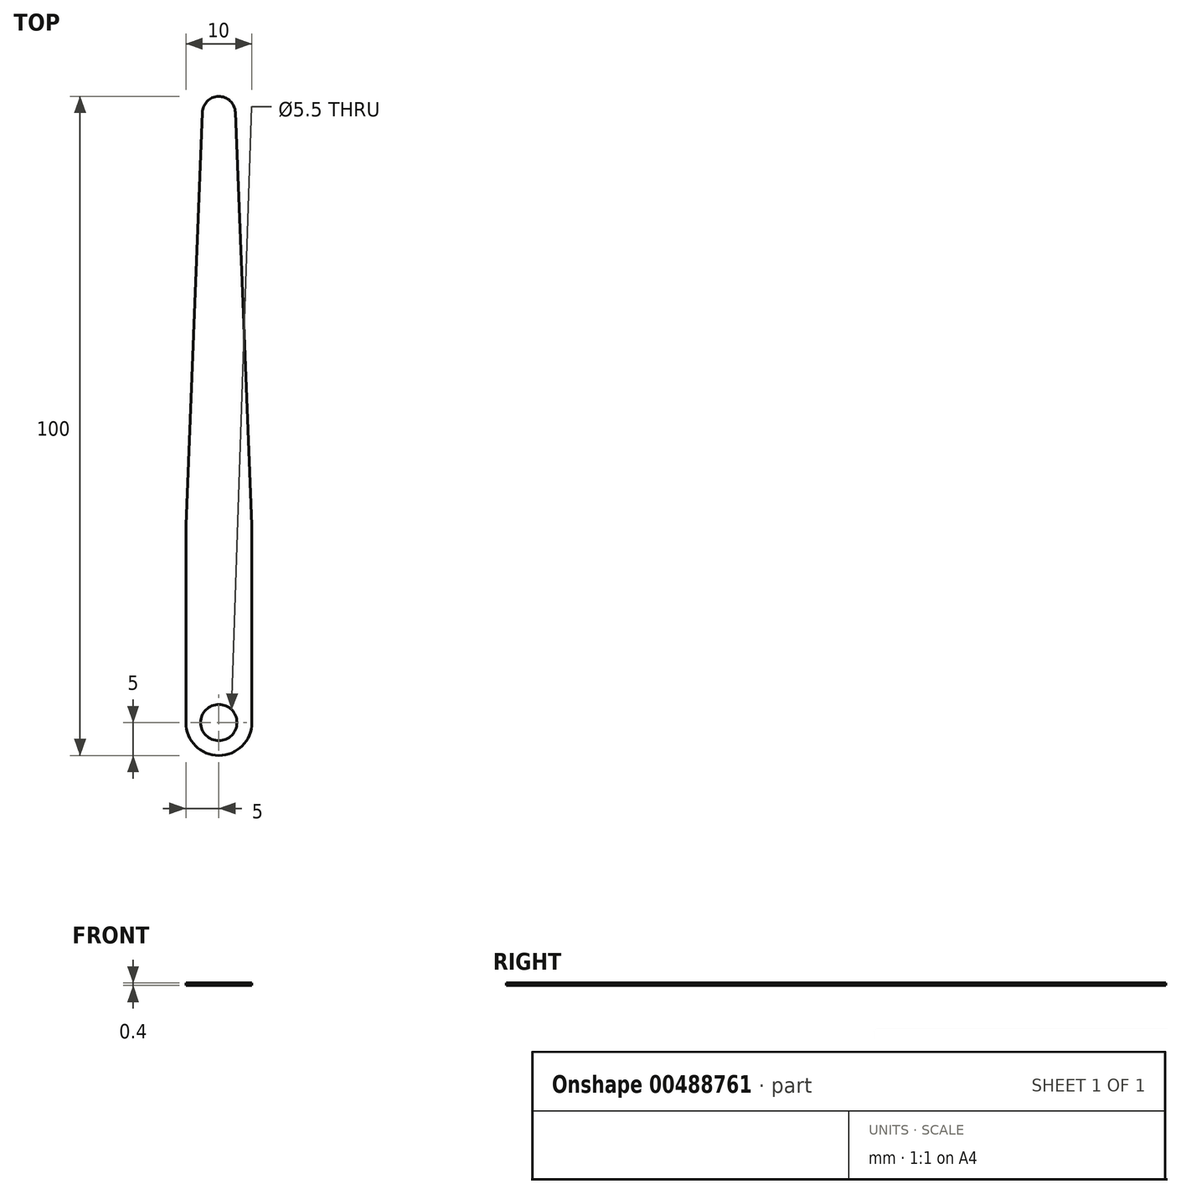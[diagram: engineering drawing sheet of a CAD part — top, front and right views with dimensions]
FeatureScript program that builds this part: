
annotation { "Feature Type Name" : "Feature", "Feature Type Description" : "" }
export const myFeature = defineFeature(function(context is Context, id is Id, definition is map)
    precondition{}
    {
        {
            var Q0;
            Q0=qCreatedBy(makeId("Top.planeOp"),FACE);
            var sketch = newSketch(context, id + "F0", { "sketchPlane" : qUnion([Q0])});
            skArc(sketch, "E0", {"start": v(-5, 0) * mm, "mid": v(0, -5) * mm, "end": v(5, 0) * mm});
            skArc(sketch, "E1", {"start": v(2.5, 92.6) * mm, "mid": v(-0.05, 95) * mm, "end": v(-2.5, 92.5) * mm});
            skCircle(sketch, "E2", {"center": v(0, 0) * mm, "radius": 2.75 * mm});
            skLineSegment(sketch, "E3.left", {"start": v(-5, 0) * mm, "end": v(-5, 30) * mm});
            skLineSegment(sketch, "E3.right", {"start": v(5, 0) * mm, "end": v(5, 30) * mm});
            skLineSegment(sketch, "E4", {"start": v(-5, 30) * mm, "end": v(-2.5, 92.5) * mm});
            skLineSegment(sketch, "E5", {"start": v(5, 30) * mm, "end": v(2.5, 92.6) * mm});
            skPoint(sketch, "E6.center.orphan", {"position": v(0, 77.5) * mm});
            skPoint(sketch, "E7.center.orphan", {"position": v(0, 62.5) * mm});
            skText(sketch, "E8", { "text": "AJ 245", "fontName": "RobotoSlab-Regular.ttf"});
            const initialGuessF0  = {"E8": [-0.02495, 0.10525, 0, -1, 0.00223]};
            skSetInitialGuess(sketch, initialGuessF0);
            skSolve(sketch);
        }
        {
            var Q0;
            Q0=makeQuery(id+"F0.imprint","IMPRINT",FACE,{"disambiguationData":[TD([[makeQuery(id+"F0.imprint","IMPRINT",EDGE,{"derivedFrom":sQuery(id+"F0.wireOp",EDGE,"E0")}),1.0]])]});
            extrude(context, id + "F1", {"entities" : qUnion([Q0]), "depth" : 0.4 * mm, "offsetDistance" : 25 * mm});
        }
    });
